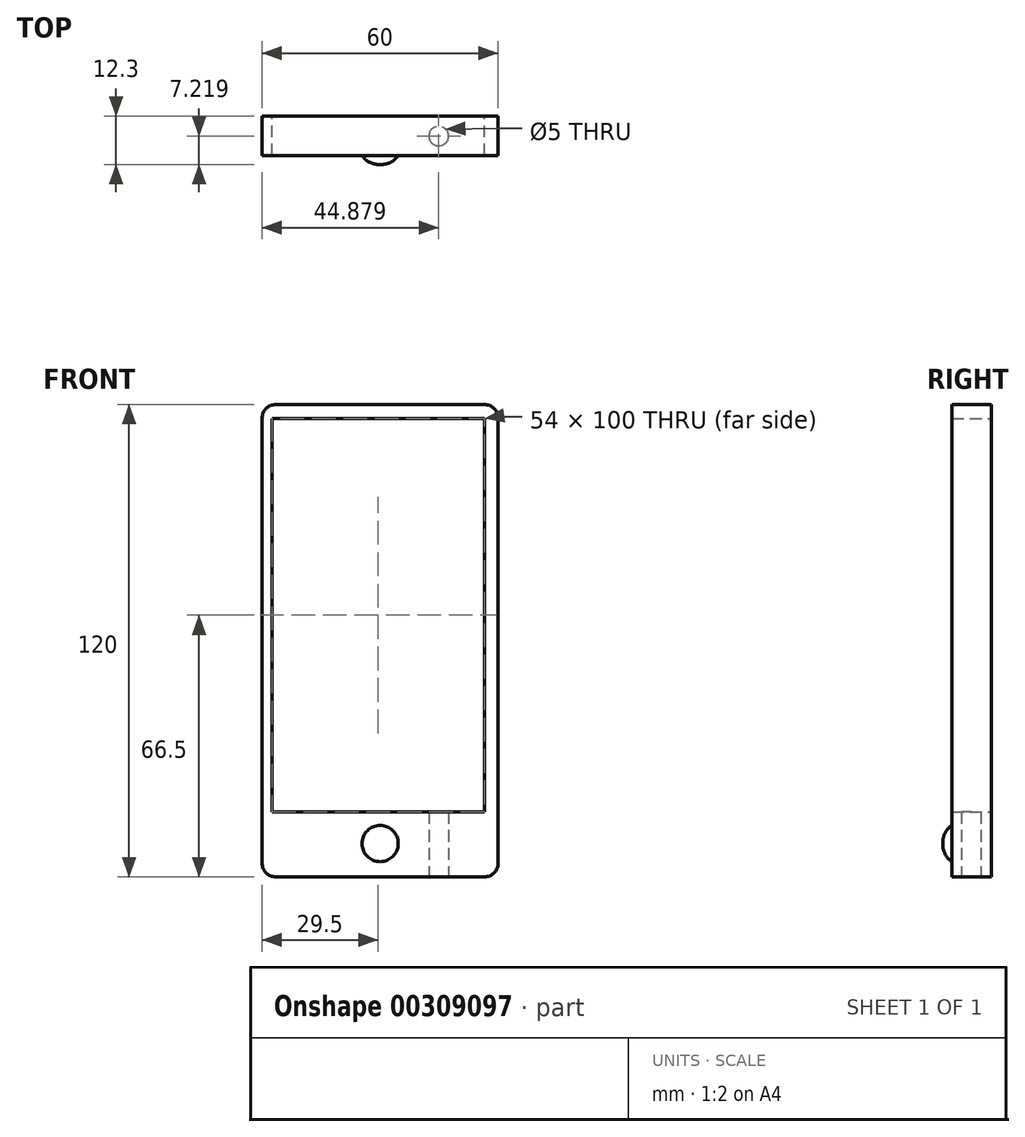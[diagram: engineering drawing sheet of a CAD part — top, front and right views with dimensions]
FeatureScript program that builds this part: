
annotation { "Feature Type Name" : "Feature", "Feature Type Description" : "" }
export const myFeature = defineFeature(function(context is Context, id is Id, definition is map)
    precondition{}
    {
        {
            var Q0;
            Q0=qCreatedBy(makeId("Front.planeOp"),FACE);
            var sketch = newSketch(context, id + "F0", { "sketchPlane" : qUnion([Q0])});
            skLineSegment(sketch, "E0.bottom", {"start": v(26.5, 60) * mm, "end": v(-26.5, 60) * mm});
            skLineSegment(sketch, "E0.top", {"start": v(26.5, -60) * mm, "end": v(-26.5, -60) * mm});
            skLineSegment(sketch, "E0.left", {"start": v(30, 56.5) * mm, "end": v(30, -56.5) * mm});
            skLineSegment(sketch, "E0.right", {"start": v(-30, 56.5) * mm, "end": v(-30, -56.5) * mm});
            skPoint(sketch, "E0.middle", {"position": v(0, 0) * mm});
            skPoint(sketch, "E1.visualSharp", {"position": v(-30, 60) * mm});
            skArc(sketch, "E1.filletArc", {"start": v(-26.5, 60) * mm, "mid": v(-28.97, 58.97) * mm, "end": v(-30, 56.5) * mm});
            skPoint(sketch, "E2.visualSharp", {"position": v(30, 60) * mm});
            skArc(sketch, "E2.filletArc", {"start": v(30, 56.5) * mm, "mid": v(28.97, 58.97) * mm, "end": v(26.5, 60) * mm});
            skPoint(sketch, "E3.visualSharp", {"position": v(30, -60) * mm});
            skArc(sketch, "E3.filletArc", {"start": v(26.5, -60) * mm, "mid": v(28.97, -58.97) * mm, "end": v(30, -56.5) * mm});
            skPoint(sketch, "E4.visualSharp", {"position": v(-30, -60) * mm});
            skArc(sketch, "E4.filletArc", {"start": v(-30, -56.5) * mm, "mid": v(-28.97, -58.97) * mm, "end": v(-26.5, -60) * mm});
            skLineSegment(sketch, "E5.bottom", {"start": v(-27.5, 56.5) * mm, "end": v(26.5, 56.5) * mm});
            skLineSegment(sketch, "E5.top", {"start": v(-27.5, -43.5) * mm, "end": v(26.5, -43.5) * mm});
            skLineSegment(sketch, "E5.left", {"start": v(-27.5, 56.5) * mm, "end": v(-27.5, -43.5) * mm});
            skLineSegment(sketch, "E5.right", {"start": v(26.5, 56.5) * mm, "end": v(26.5, -43.5) * mm});
            skSolve(sketch);
        }
        {
            var Q0;
            Q0 = qSketchRegion(id + "F0", true);
            extrude(context, id + "F1", {"entities" : qUnion([Q0]), "depth" : 10 * mm});
        }
        {
            var Q0;
            Q0=makeQuery(id+"F1.opExtrude","CAP_FACE",FACE,{"disambiguationData":[OSD([sQuery(id+"F0.wireOp",EDGE,"E0.bottom"),sQuery(id+"F0.wireOp",EDGE,"E0.top"),sQuery(id+"F0.wireOp",EDGE,"E0.left"),sQuery(id+"F0.wireOp",EDGE,"E0.right"),sQuery(id+"F0.wireOp",EDGE,"E1.filletArc"),sQuery(id+"F0.wireOp",EDGE,"E2.filletArc"),sQuery(id+"F0.wireOp",EDGE,"E3.filletArc"),sQuery(id+"F0.wireOp",EDGE,"E4.filletArc"),sQuery(id+"F0.wireOp",EDGE,"E5.bottom"),sQuery(id+"F0.wireOp",EDGE,"E5.top"),sQuery(id+"F0.wireOp",EDGE,"E5.left"),sQuery(id+"F0.wireOp",EDGE,"E5.right")])],"isStart":false});
            var sketch = newSketch(context, id + "F2", { "sketchPlane" : qUnion([Q0])});
            skCircle(sketch, "E6", {"center": v(0, -51.53) * mm, "radius": 4.6 * mm});
            skSolve(sketch);
        }
        {
            var Q0;
            Q0 = qSketchRegion(id + "F2", true);
            extrude(context, id + "F3", {"entities" : qUnion([Q0]), "operationType" : NewBodyOperationType.ADD, "depth" : 2.3 * mm, "offsetDistance" : 25 * mm});
        }
        {
            var Q0;
            Q0=makeQuery(id+"F3.opExtrude","CAP_FACE",FACE,{"disambiguationData":[OSD([sQuery(id+"F2.wireOp",EDGE,"E6")])],"isStart":false});
            fillet(context, id + "F4", {"entities" : qUnion([Q0]), "radius" : 5.07 * mm, "tangentPropagation" : true, "allowEdgeOverflow" : false});
        }
        {
            var Q0;
            Q0=makeQuery(id+"F1.opExtrude","SWEPT_FACE",FACE,{"disambiguationData":[OSD([sQuery(id+"F0.wireOp",EDGE,"E0.top")])]});
            var sketch = newSketch(context, id + "F5", { "sketchPlane" : qUnion([Q0])});
            skLineSegment(sketch, "E7.bottom", {"start": v(-16.7, 6.9) * mm, "end": v(3.81, 6.9) * mm});
            skLineSegment(sketch, "E7.top", {"start": v(-16.7, 2.9) * mm, "end": v(3.81, 2.9) * mm});
            skLineSegment(sketch, "E7.left", {"start": v(-16.7, 6.9) * mm, "end": v(-16.7, 2.9) * mm});
            skLineSegment(sketch, "E7.right", {"start": v(3.81, 6.9) * mm, "end": v(3.81, 2.9) * mm});
            skCircle(sketch, "E8", {"center": v(14.88, 5.08) * mm, "radius": 2.18 * mm});
            skSolve(sketch);
        }
        {
            var Q0;
            Q0=sQuery(id+"F5.wireOp",VERTEX,"E8.center");
            var Q1;
            Q1=makeQuery(id+"F1.opExtrude","SWEPT_BODY",BODY,{"disambiguationData":[OSD([sQuery(id+"F0.wireOp",EDGE,"E0.bottom"),sQuery(id+"F0.wireOp",EDGE,"E0.top"),sQuery(id+"F0.wireOp",EDGE,"E0.left"),sQuery(id+"F0.wireOp",EDGE,"E0.right"),sQuery(id+"F0.wireOp",EDGE,"E1.filletArc"),sQuery(id+"F0.wireOp",EDGE,"E2.filletArc"),sQuery(id+"F0.wireOp",EDGE,"E3.filletArc"),sQuery(id+"F0.wireOp",EDGE,"E4.filletArc"),sQuery(id+"F0.wireOp",EDGE,"E5.bottom"),sQuery(id+"F0.wireOp",EDGE,"E5.top"),sQuery(id+"F0.wireOp",EDGE,"E5.left"),sQuery(id+"F0.wireOp",EDGE,"E5.right")])]});
            hole(context, id + "F6", {"style" : HoleStyle.SIMPLE, "endStyle" : HoleEndStyle.BLIND, "holeDiameter" : 5 * mm, "holeDepth" : 44 * mm, "isTappedThrough" : true, "tappedDepth" : 12 * mm, "tapClearance" : 3, "locations" : qUnion([Q0]), "scope" : qUnion([Q1])});
        }
    });
